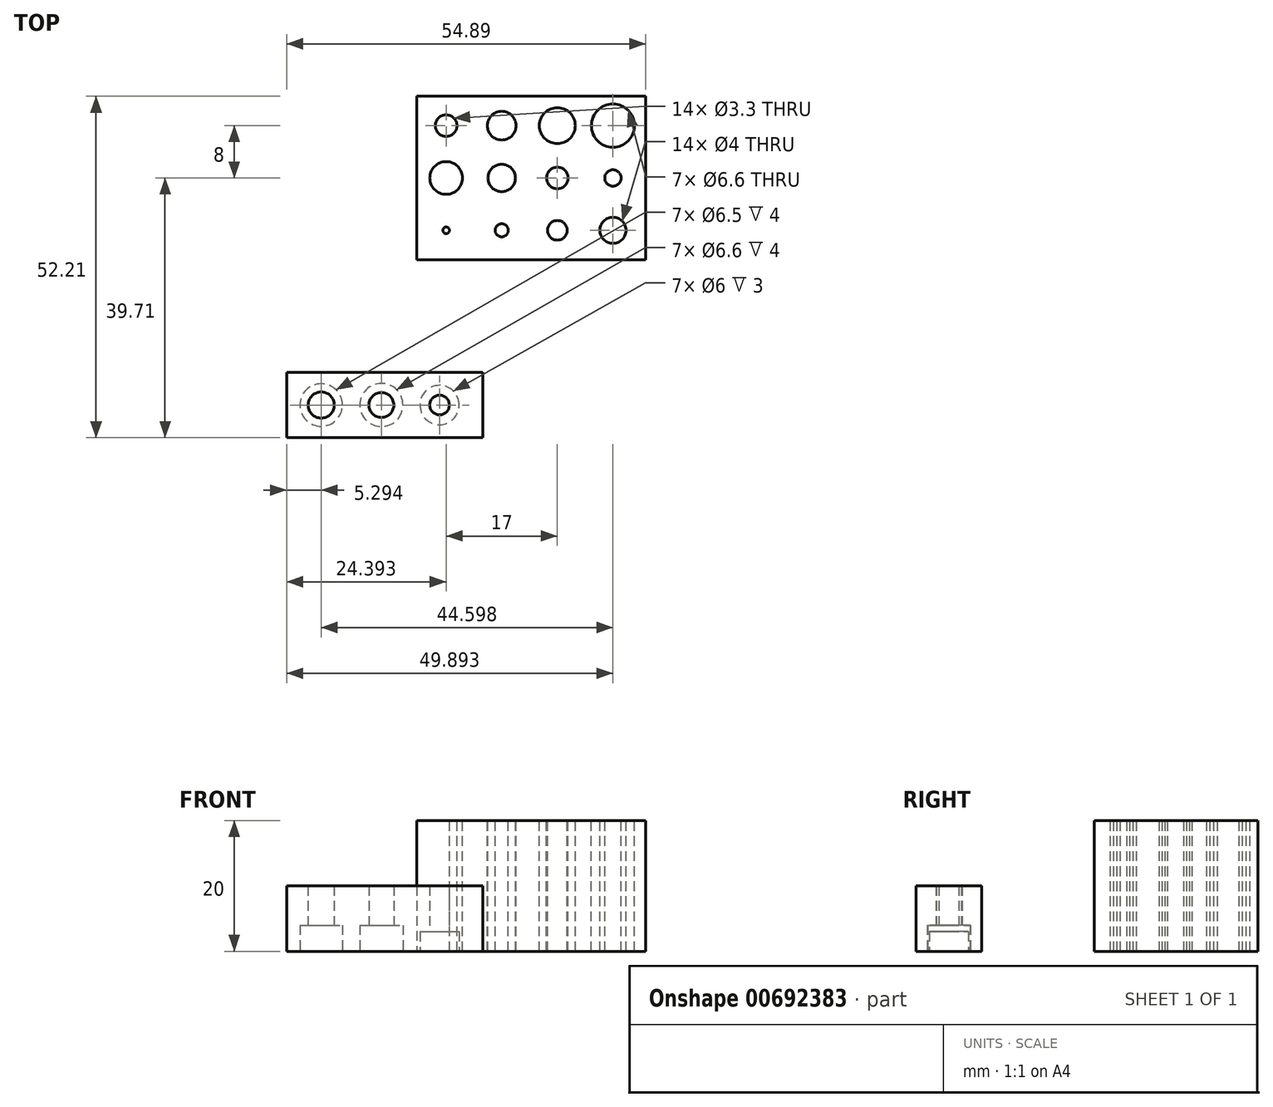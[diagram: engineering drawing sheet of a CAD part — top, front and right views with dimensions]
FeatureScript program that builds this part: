
annotation { "Feature Type Name" : "Feature", "Feature Type Description" : "" }
export const myFeature = defineFeature(function(context is Context, id is Id, definition is map)
    precondition{}
    {
        {
            var Q0;
            Q0=qCreatedBy(makeId("Top.planeOp"),FACE);
            var sketch = newSketch(context, id + "F0", { "sketchPlane" : qUnion([Q0])});
            skLineSegment(sketch, "E0.bottom", {"start": v(-19.28, 12.5) * mm, "end": v(15.72, 12.5) * mm});
            skLineSegment(sketch, "E0.top", {"start": v(-19.28, -12.5) * mm, "end": v(15.72, -12.5) * mm});
            skLineSegment(sketch, "E0.left", {"start": v(-19.28, 12.5) * mm, "end": v(-19.28, -12.5) * mm});
            skLineSegment(sketch, "E0.right", {"start": v(15.72, 12.5) * mm, "end": v(15.72, -12.5) * mm});
            skSolve(sketch);
        }
        {
            var Q0;
            Q0 = qSketchRegion(id + "F0", true);
            extrude(context, id + "F1", {"entities" : qUnion([Q0]), "depth" : 20 * mm, "offsetDistance" : 25 * mm});
        }
        {
            var Q0;
            Q0=makeQuery(id+"F1.opExtrude","CAP_FACE",FACE,{"disambiguationData":[OSD([sQuery(id+"F0.wireOp",EDGE,"E0.bottom"),sQuery(id+"F0.wireOp",EDGE,"E0.top"),sQuery(id+"F0.wireOp",EDGE,"E0.left"),sQuery(id+"F0.wireOp",EDGE,"E0.right")])],"isStart":false});
            var sketch = newSketch(context, id + "F2", { "sketchPlane" : qUnion([Q0])});
            skPoint(sketch, "E1", {"position": v(-14.78, 8) * mm});
            skLineSegment(sketch, "E2.0", {"start": v(-19.28, 12.5) * mm, "end": v(15.72, 12.5) * mm});
            skPoint(sketch, "E3.0.1.0", {"position": v(-14.78, 0) * mm});
            skPoint(sketch, "E3.0.2.0", {"position": v(-14.78, -8) * mm});
            skPoint(sketch, "E3.1.0.0", {"position": v(-6.28, 8) * mm});
            skPoint(sketch, "E3.1.1.0", {"position": v(-6.28, 0) * mm});
            skPoint(sketch, "E3.1.2.0", {"position": v(-6.28, -8) * mm});
            skPoint(sketch, "E3.2.0.0", {"position": v(2.22, 8) * mm});
            skPoint(sketch, "E3.2.1.0", {"position": v(2.22, 0) * mm});
            skPoint(sketch, "E3.2.2.0", {"position": v(2.22, -8) * mm});
            skPoint(sketch, "E3.3.0.0", {"position": v(10.72, 8) * mm});
            skPoint(sketch, "E3.3.1.0", {"position": v(10.72, 0) * mm});
            skPoint(sketch, "E3.3.2.0", {"position": v(10.72, -8) * mm});
            skLineSegment(sketch, "E3.direction1", {"start": v(-14.78, 8) * mm, "end": v(-6.28, 8) * mm, "construction": true});
            skLineSegment(sketch, "E3.direction2", {"start": v(-14.78, 8) * mm, "end": v(-14.78, 0) * mm, "construction": true});
            skSolve(sketch);
        }
        {
            var Q0;
            Q0=sQuery(id+"F2.wireOp",VERTEX,"E1");
            var Q1;
            Q1=makeQuery(id+"F1.opExtrude","SWEPT_BODY",BODY,{"disambiguationData":[OSD([sQuery(id+"F0.wireOp",EDGE,"E0.bottom"),sQuery(id+"F0.wireOp",EDGE,"E0.top"),sQuery(id+"F0.wireOp",EDGE,"E0.left"),sQuery(id+"F0.wireOp",EDGE,"E0.right")])]});
            hole(context, id + "F3", {"style" : HoleStyle.SIMPLE, "endStyle" : HoleEndStyle.THROUGH, "standardTappedOrClearance" : lookupTablePath({ "standard" : "ISO", "fit" : "Normal", "size" : "M3", "type" : "Clearance" }), "standardBlindInLast" : lookupTablePath({ "fit" : "Standard", "standard" : "ISO", "size" : "M3", "type" : "Clearance" }), "holeDiameter" : 3.3 * mm, "majorDiameter" : 5 * mm, "isTappedThrough" : true, "tappedDepth" : 12 * mm, "tapClearance" : 3, "locations" : qUnion([Q0]), "scope" : qUnion([Q1])});
        }
        {
            var Q0;
            Q0=sQuery(id+"F2.wireOp",VERTEX,"E3.direction1.end");
            var Q1;
            Q1=makeQuery(id+"F1.opExtrude","SWEPT_BODY",BODY,{"disambiguationData":[OSD([sQuery(id+"F0.wireOp",EDGE,"E0.bottom"),sQuery(id+"F0.wireOp",EDGE,"E0.top"),sQuery(id+"F0.wireOp",EDGE,"E0.left"),sQuery(id+"F0.wireOp",EDGE,"E0.right")])]});
            hole(context, id + "F4", {"style" : HoleStyle.SIMPLE, "endStyle" : HoleEndStyle.THROUGH, "standardTappedOrClearance" : lookupTablePath({ "standard" : "ISO", "fit" : "Normal", "size" : "M4", "type" : "Clearance" }), "standardBlindInLast" : lookupTablePath({ "fit" : "Standard", "standard" : "ISO", "size" : "M4", "type" : "Clearance" }), "holeDiameter" : 4.4 * mm, "majorDiameter" : 5 * mm, "isTappedThrough" : true, "tappedDepth" : 12 * mm, "tapClearance" : 3, "locations" : qUnion([Q0]), "scope" : qUnion([Q1])});
        }
        {
            var Q0;
            Q0=sQuery(id+"F2.wireOp",VERTEX,"E3.2.0.0");
            var Q1;
            Q1=makeQuery(id+"F1.opExtrude","SWEPT_BODY",BODY,{"disambiguationData":[OSD([sQuery(id+"F0.wireOp",EDGE,"E0.bottom"),sQuery(id+"F0.wireOp",EDGE,"E0.top"),sQuery(id+"F0.wireOp",EDGE,"E0.left"),sQuery(id+"F0.wireOp",EDGE,"E0.right")])]});
            hole(context, id + "F5", {"style" : HoleStyle.SIMPLE, "endStyle" : HoleEndStyle.THROUGH, "standardTappedOrClearance" : lookupTablePath({ "standard" : "ISO", "fit" : "Normal", "size" : "M5", "type" : "Clearance" }), "standardBlindInLast" : lookupTablePath({ "fit" : "Standard", "standard" : "ISO", "size" : "M5", "type" : "Clearance" }), "holeDiameter" : 5.5 * mm, "majorDiameter" : 5 * mm, "isTappedThrough" : true, "tappedDepth" : 12 * mm, "tapClearance" : 3, "locations" : qUnion([Q0]), "scope" : qUnion([Q1])});
        }
        {
            var Q0;
            Q0=sQuery(id+"F2.wireOp",VERTEX,"E3.3.0.0");
            var Q1;
            Q1=makeQuery(id+"F1.opExtrude","SWEPT_BODY",BODY,{"disambiguationData":[OSD([sQuery(id+"F0.wireOp",EDGE,"E0.bottom"),sQuery(id+"F0.wireOp",EDGE,"E0.top"),sQuery(id+"F0.wireOp",EDGE,"E0.left"),sQuery(id+"F0.wireOp",EDGE,"E0.right")])]});
            hole(context, id + "F6", {"style" : HoleStyle.SIMPLE, "endStyle" : HoleEndStyle.THROUGH, "standardTappedOrClearance" : lookupTablePath({ "standard" : "ISO", "fit" : "Normal", "size" : "M6", "type" : "Clearance" }), "standardBlindInLast" : lookupTablePath({ "fit" : "Standard", "standard" : "ISO", "size" : "M6", "type" : "Clearance" }), "holeDiameter" : 6.6 * mm, "majorDiameter" : 5 * mm, "isTappedThrough" : true, "tappedDepth" : 12 * mm, "tapClearance" : 3, "locations" : qUnion([Q0]), "scope" : qUnion([Q1])});
        }
        {
            var Q0;
            Q0=sQuery(id+"F2.wireOp",VERTEX,"E3.0.1.0");
            var Q1;
            Q1=makeQuery(id+"F1.opExtrude","SWEPT_BODY",BODY,{"disambiguationData":[OSD([sQuery(id+"F0.wireOp",EDGE,"E0.bottom"),sQuery(id+"F0.wireOp",EDGE,"E0.top"),sQuery(id+"F0.wireOp",EDGE,"E0.left"),sQuery(id+"F0.wireOp",EDGE,"E0.right")])]});
            hole(context, id + "F7", {"style" : HoleStyle.SIMPLE, "endStyle" : HoleEndStyle.THROUGH, "standardTappedOrClearance" : lookupTablePath({ "standard" : "ISO", "engagement" : "75%", "pitch" : "1 mm", "size" : "M6", "type" : "Tapped" }), "standardBlindInLast" : lookupTablePath({ "standard" : "ISO", "engagement" : "75%", "pitch" : "1 mm", "size" : "M6", "type" : "Tapped" }), "holeDiameter" : 5 * mm, "majorDiameter" : 6 * mm, "showTappedDepth" : true, "isTappedThrough" : true, "tappedDepth" : 12 * mm, "tapClearance" : 3, "locations" : qUnion([Q0]), "scope" : qUnion([Q1])});
        }
        {
            var Q0;
            Q0=sQuery(id+"F2.wireOp",VERTEX,"E3.1.1.0");
            var Q1;
            Q1=makeQuery(id+"F1.opExtrude","SWEPT_BODY",BODY,{"disambiguationData":[OSD([sQuery(id+"F0.wireOp",EDGE,"E0.bottom"),sQuery(id+"F0.wireOp",EDGE,"E0.top"),sQuery(id+"F0.wireOp",EDGE,"E0.left"),sQuery(id+"F0.wireOp",EDGE,"E0.right")])]});
            hole(context, id + "F8", {"style" : HoleStyle.SIMPLE, "endStyle" : HoleEndStyle.THROUGH, "standardTappedOrClearance" : lookupTablePath({ "standard" : "ISO", "engagement" : "75%", "pitch" : "0.8 mm", "size" : "M5", "type" : "Tapped" }), "standardBlindInLast" : lookupTablePath({ "standard" : "ISO", "engagement" : "75%", "pitch" : "0.8 mm", "size" : "M5", "type" : "Tapped" }), "holeDiameter" : 4.2 * mm, "majorDiameter" : 5 * mm, "showTappedDepth" : true, "isTappedThrough" : true, "tappedDepth" : 12 * mm, "tapClearance" : 3, "locations" : qUnion([Q0]), "scope" : qUnion([Q1])});
        }
        {
            var Q0;
            Q0=sQuery(id+"F2.wireOp",VERTEX,"E3.2.1.0");
            var Q1;
            Q1=makeQuery(id+"F1.opExtrude","SWEPT_BODY",BODY,{"disambiguationData":[OSD([sQuery(id+"F0.wireOp",EDGE,"E0.bottom"),sQuery(id+"F0.wireOp",EDGE,"E0.top"),sQuery(id+"F0.wireOp",EDGE,"E0.left"),sQuery(id+"F0.wireOp",EDGE,"E0.right")])]});
            hole(context, id + "F9", {"style" : HoleStyle.SIMPLE, "endStyle" : HoleEndStyle.THROUGH, "standardTappedOrClearance" : lookupTablePath({ "standard" : "ISO", "engagement" : "75%", "pitch" : "0.7 mm", "size" : "M4", "type" : "Tapped" }), "standardBlindInLast" : lookupTablePath({ "standard" : "ISO", "engagement" : "75%", "pitch" : "0.7 mm", "size" : "M4", "type" : "Tapped" }), "holeDiameter" : 3.3 * mm, "majorDiameter" : 4 * mm, "showTappedDepth" : true, "isTappedThrough" : true, "tappedDepth" : 12 * mm, "tapClearance" : 3, "locations" : qUnion([Q0]), "scope" : qUnion([Q1])});
        }
        {
            var Q0;
            Q0=sQuery(id+"F2.wireOp",VERTEX,"E3.3.1.0");
            var Q1;
            Q1=makeQuery(id+"F1.opExtrude","SWEPT_BODY",BODY,{"disambiguationData":[OSD([sQuery(id+"F0.wireOp",EDGE,"E0.bottom"),sQuery(id+"F0.wireOp",EDGE,"E0.top"),sQuery(id+"F0.wireOp",EDGE,"E0.left"),sQuery(id+"F0.wireOp",EDGE,"E0.right")])]});
            hole(context, id + "F10", {"style" : HoleStyle.SIMPLE, "endStyle" : HoleEndStyle.THROUGH, "standardTappedOrClearance" : lookupTablePath({ "standard" : "ISO", "engagement" : "75%", "pitch" : "0.5 mm", "size" : "M3", "type" : "Tapped" }), "standardBlindInLast" : lookupTablePath({ "standard" : "ISO", "engagement" : "75%", "pitch" : "0.5 mm", "size" : "M3", "type" : "Tapped" }), "holeDiameter" : 2.5 * mm, "majorDiameter" : 3 * mm, "showTappedDepth" : true, "isTappedThrough" : true, "tappedDepth" : 12 * mm, "tapClearance" : 3, "locations" : qUnion([Q0]), "scope" : qUnion([Q1])});
        }
        {
            var Q0;
            Q0=sQuery(id+"F2.wireOp",VERTEX,"E3.0.2.0");
            var Q1;
            Q1=makeQuery(id+"F1.opExtrude","SWEPT_BODY",BODY,{"disambiguationData":[OSD([sQuery(id+"F0.wireOp",EDGE,"E0.bottom"),sQuery(id+"F0.wireOp",EDGE,"E0.top"),sQuery(id+"F0.wireOp",EDGE,"E0.left"),sQuery(id+"F0.wireOp",EDGE,"E0.right")])]});
            hole(context, id + "F11", {"style" : HoleStyle.SIMPLE, "endStyle" : HoleEndStyle.THROUGH, "standardTappedOrClearance" : lookupTablePath({ "standard" : "ISO", "size" : "1", "type" : "Drilled" }), "standardBlindInLast" : lookupTablePath({ "standard" : "ISO", "size" : "1", "type" : "Drilled" }), "holeDiameter" : 1 * mm, "majorDiameter" : 3 * mm, "isTappedThrough" : true, "tappedDepth" : 12 * mm, "tapClearance" : 3, "locations" : qUnion([Q0]), "scope" : qUnion([Q1])});
        }
        {
            var Q0;
            Q0=sQuery(id+"F2.wireOp",VERTEX,"E3.1.2.0");
            var Q1;
            Q1=makeQuery(id+"F1.opExtrude","SWEPT_BODY",BODY,{"disambiguationData":[OSD([sQuery(id+"F0.wireOp",EDGE,"E0.bottom"),sQuery(id+"F0.wireOp",EDGE,"E0.top"),sQuery(id+"F0.wireOp",EDGE,"E0.left"),sQuery(id+"F0.wireOp",EDGE,"E0.right")])]});
            hole(context, id + "F12", {"style" : HoleStyle.SIMPLE, "endStyle" : HoleEndStyle.THROUGH, "standardTappedOrClearance" : lookupTablePath({ "standard" : "ISO", "size" : "2", "type" : "Drilled" }), "standardBlindInLast" : lookupTablePath({ "standard" : "ISO", "size" : "2", "type" : "Drilled" }), "holeDiameter" : 2 * mm, "majorDiameter" : 5 * mm, "isTappedThrough" : true, "tappedDepth" : 12 * mm, "tapClearance" : 3, "locations" : qUnion([Q0]), "scope" : qUnion([Q1])});
        }
        {
            var Q0;
            Q0=sQuery(id+"F2.wireOp",VERTEX,"E3.2.2.0");
            var Q1;
            Q1=makeQuery(id+"F1.opExtrude","SWEPT_BODY",BODY,{"disambiguationData":[OSD([sQuery(id+"F0.wireOp",EDGE,"E0.bottom"),sQuery(id+"F0.wireOp",EDGE,"E0.top"),sQuery(id+"F0.wireOp",EDGE,"E0.left"),sQuery(id+"F0.wireOp",EDGE,"E0.right")])]});
            hole(context, id + "F13", {"style" : HoleStyle.SIMPLE, "endStyle" : HoleEndStyle.THROUGH, "standardTappedOrClearance" : lookupTablePath({ "standard" : "ISO", "size" : "3", "type" : "Drilled" }), "standardBlindInLast" : lookupTablePath({ "standard" : "ISO", "size" : "3", "type" : "Drilled" }), "holeDiameter" : 3 * mm, "majorDiameter" : 5 * mm, "isTappedThrough" : true, "tappedDepth" : 12 * mm, "tapClearance" : 3, "locations" : qUnion([Q0]), "scope" : qUnion([Q1])});
        }
        {
            var Q0;
            Q0=sQuery(id+"F2.wireOp",VERTEX,"E3.3.2.0");
            var Q1;
            Q1=makeQuery(id+"F1.opExtrude","SWEPT_BODY",BODY,{"disambiguationData":[OSD([sQuery(id+"F0.wireOp",EDGE,"E0.bottom"),sQuery(id+"F0.wireOp",EDGE,"E0.top"),sQuery(id+"F0.wireOp",EDGE,"E0.left"),sQuery(id+"F0.wireOp",EDGE,"E0.right")])]});
            hole(context, id + "F14", {"style" : HoleStyle.SIMPLE, "endStyle" : HoleEndStyle.THROUGH, "standardTappedOrClearance" : lookupTablePath({ "standard" : "ISO", "size" : "4", "type" : "Drilled" }), "standardBlindInLast" : lookupTablePath({ "standard" : "ISO", "size" : "4", "type" : "Drilled" }), "holeDiameter" : 4 * mm, "majorDiameter" : 5 * mm, "isTappedThrough" : true, "tappedDepth" : 12 * mm, "tapClearance" : 3, "locations" : qUnion([Q0]), "scope" : qUnion([Q1])});
        }
        {
            var Q0;
            Q0=qCreatedBy(makeId("Top.planeOp"),FACE);
            var sketch = newSketch(context, id + "F15", { "sketchPlane" : qUnion([Q0])});
            skLineSegment(sketch, "E4.bottom", {"start": v(-39.17, -29.7) * mm, "end": v(-9.17, -29.7) * mm});
            skLineSegment(sketch, "E4.top", {"start": v(-39.17, -39.7) * mm, "end": v(-9.17, -39.7) * mm});
            skLineSegment(sketch, "E4.left", {"start": v(-39.17, -29.7) * mm, "end": v(-39.17, -39.7) * mm});
            skLineSegment(sketch, "E4.right", {"start": v(-9.17, -29.7) * mm, "end": v(-9.17, -39.7) * mm});
            skPoint(sketch, "E5", {"position": v(-33.88, -34.7) * mm});
            skPoint(sketch, "E5.positionSnap0", {"position": v(-39.17, -34.7) * mm});
            skPoint(sketch, "E6", {"position": v(-24.68, -34.7) * mm});
            skPoint(sketch, "E7", {"position": v(-15.79, -34.7) * mm});
            skSolve(sketch);
        }
        {
            var Q0;
            Q0=makeQuery(id+"F15.imprint","IMPRINT",FACE,{"disambiguationData":[TD([[makeQuery(id+"F15.imprint","IMPRINT",EDGE,{"derivedFrom":sQuery(id+"F15.wireOp",EDGE,"E4.bottom")}),-1.0]])]});
            extrude(context, id + "F16", {"entities" : qUnion([Q0]), "depth" : 10 * mm, "offsetDistance" : 25 * mm});
        }
        {
            var Q0;
            Q0=sQuery(id+"F15.wireOp",VERTEX,"E5");
            var Q1;
            Q1=makeQuery(id+"F16.opExtrude","SWEPT_BODY",BODY,{"disambiguationData":[OSD([sQuery(id+"F15.wireOp",EDGE,"E4.bottom"),sQuery(id+"F15.wireOp",EDGE,"E4.top"),sQuery(id+"F15.wireOp",EDGE,"E4.left"),sQuery(id+"F15.wireOp",EDGE,"E4.right")])]});
            hole(context, id + "F17", {"style" : HoleStyle.C_BORE, "endStyle" : HoleEndStyle.THROUGH, "oppositeDirection" : true, "standardTappedOrClearance" : lookupTablePath({ "standard" : "ISO", "size" : "4", "type" : "Drilled" }), "standardBlindInLast" : lookupTablePath({ "standard" : "ISO", "size" : "4", "type" : "Drilled" }), "holeDiameter" : 4 * mm, "cBoreDiameter" : 6.5 * mm, "cBoreDepth" : 4 * mm, "majorDiameter" : 5 * mm, "isTappedThrough" : true, "tappedDepth" : 12 * mm, "tapClearance" : 3, "locations" : qUnion([Q0]), "scope" : qUnion([Q1])});
        }
        {
            var Q0;
            Q0=sQuery(id+"F15.wireOp",VERTEX,"E6");
            var Q1;
            Q1=makeQuery(id+"F16.opExtrude","SWEPT_BODY",BODY,{"disambiguationData":[OSD([sQuery(id+"F15.wireOp",EDGE,"E4.bottom"),sQuery(id+"F15.wireOp",EDGE,"E4.top"),sQuery(id+"F15.wireOp",EDGE,"E4.left"),sQuery(id+"F15.wireOp",EDGE,"E4.right")])]});
            hole(context, id + "F18", {"style" : HoleStyle.C_BORE, "endStyle" : HoleEndStyle.THROUGH, "oppositeDirection" : true, "holeDiameter" : 3.8 * mm, "cBoreDiameter" : 6.6 * mm, "cBoreDepth" : 4 * mm, "majorDiameter" : 5 * mm, "isTappedThrough" : true, "tappedDepth" : 12 * mm, "tapClearance" : 3, "locations" : qUnion([Q0]), "scope" : qUnion([Q1])});
        }
        {
            var Q0;
            Q0=sQuery(id+"F15.wireOp",VERTEX,"E7");
            var Q1;
            Q1=makeQuery(id+"F16.opExtrude","SWEPT_BODY",BODY,{"disambiguationData":[OSD([sQuery(id+"F15.wireOp",EDGE,"E4.bottom"),sQuery(id+"F15.wireOp",EDGE,"E4.top"),sQuery(id+"F15.wireOp",EDGE,"E4.left"),sQuery(id+"F15.wireOp",EDGE,"E4.right")])]});
            hole(context, id + "F19", {"style" : HoleStyle.C_BORE, "endStyle" : HoleEndStyle.THROUGH, "oppositeDirection" : true, "standardTappedOrClearance" : lookupTablePath({ "standard" : "ISO", "size" : "3", "type" : "Drilled" }), "standardBlindInLast" : lookupTablePath({ "standard" : "ISO", "size" : "3", "type" : "Drilled" }), "holeDiameter" : 3 * mm, "cBoreDiameter" : 6 * mm, "cBoreDepth" : 3 * mm, "majorDiameter" : 5 * mm, "isTappedThrough" : true, "tappedDepth" : 12 * mm, "tapClearance" : 3, "locations" : qUnion([Q0]), "scope" : qUnion([Q1])});
        }
    });
